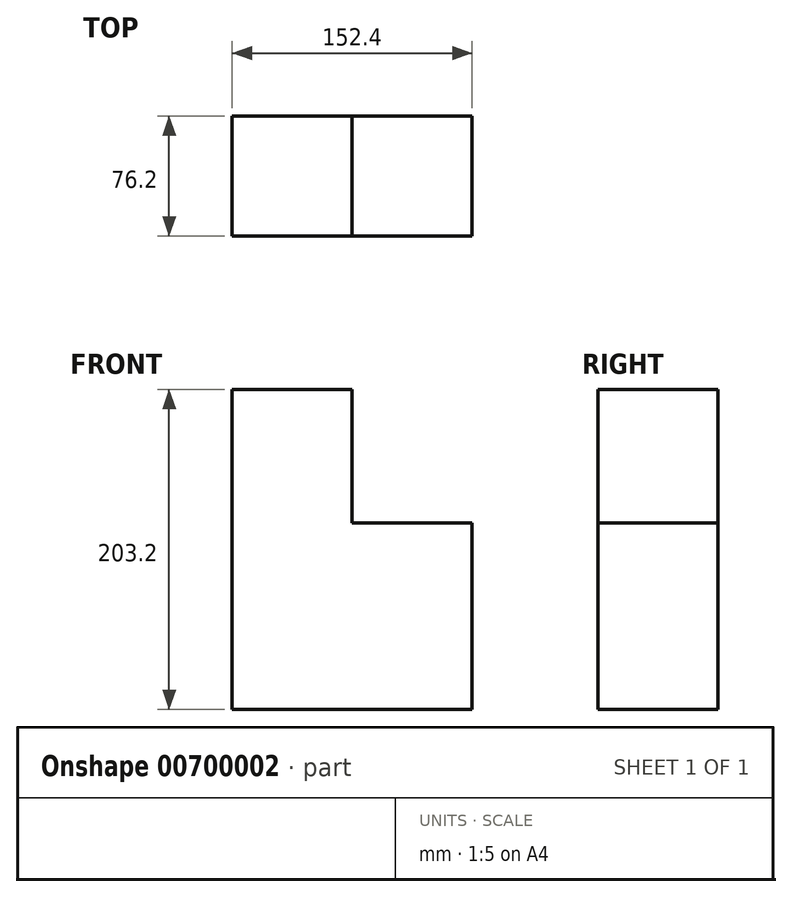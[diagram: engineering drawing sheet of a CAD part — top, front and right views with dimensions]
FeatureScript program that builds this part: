
annotation { "Feature Type Name" : "Feature", "Feature Type Description" : "" }
export const myFeature = defineFeature(function(context is Context, id is Id, definition is map)
    precondition{}
    {
        {
            var Q0;
            Q0=qCreatedBy(makeId("Front.planeOp"),FACE);
            var sketch = newSketch(context, id + "F0", { "sketchPlane" : qUnion([Q0])});
            skLineSegment(sketch, "E0", {"start": v(-76.2, 101.07) * mm, "end": v(-76.2, -102.13) * mm});
            skLineSegment(sketch, "E1", {"start": v(-76.2, -102.13) * mm, "end": v(76.2, -102.13) * mm});
            skLineSegment(sketch, "E2", {"start": v(76.2, -102.13) * mm, "end": v(76.2, 16.32) * mm});
            skLineSegment(sketch, "E3", {"start": v(76.2, 16.32) * mm, "end": v(0, 16.32) * mm});
            skLineSegment(sketch, "E4", {"start": v(0, 16.32) * mm, "end": v(0, 101.07) * mm});
            skLineSegment(sketch, "E5", {"start": v(0, 101.07) * mm, "end": v(-76.2, 101.07) * mm});
            skSolve(sketch);
        }
        {
            var Q0;
            Q0=makeQuery(id+"F0.imprint","IMPRINT",FACE,{"disambiguationData":[TD([[makeQuery(id+"F0.imprint","IMPRINT",EDGE,{"derivedFrom":sQuery(id+"F0.wireOp",EDGE,"E0")}),1.0]])]});
            extrude(context, id + "F1", {"entities" : qUnion([Q0]), "depth" : 76.2 * mm, "offsetDistance" : 25.4 * mm});
        }
    });
